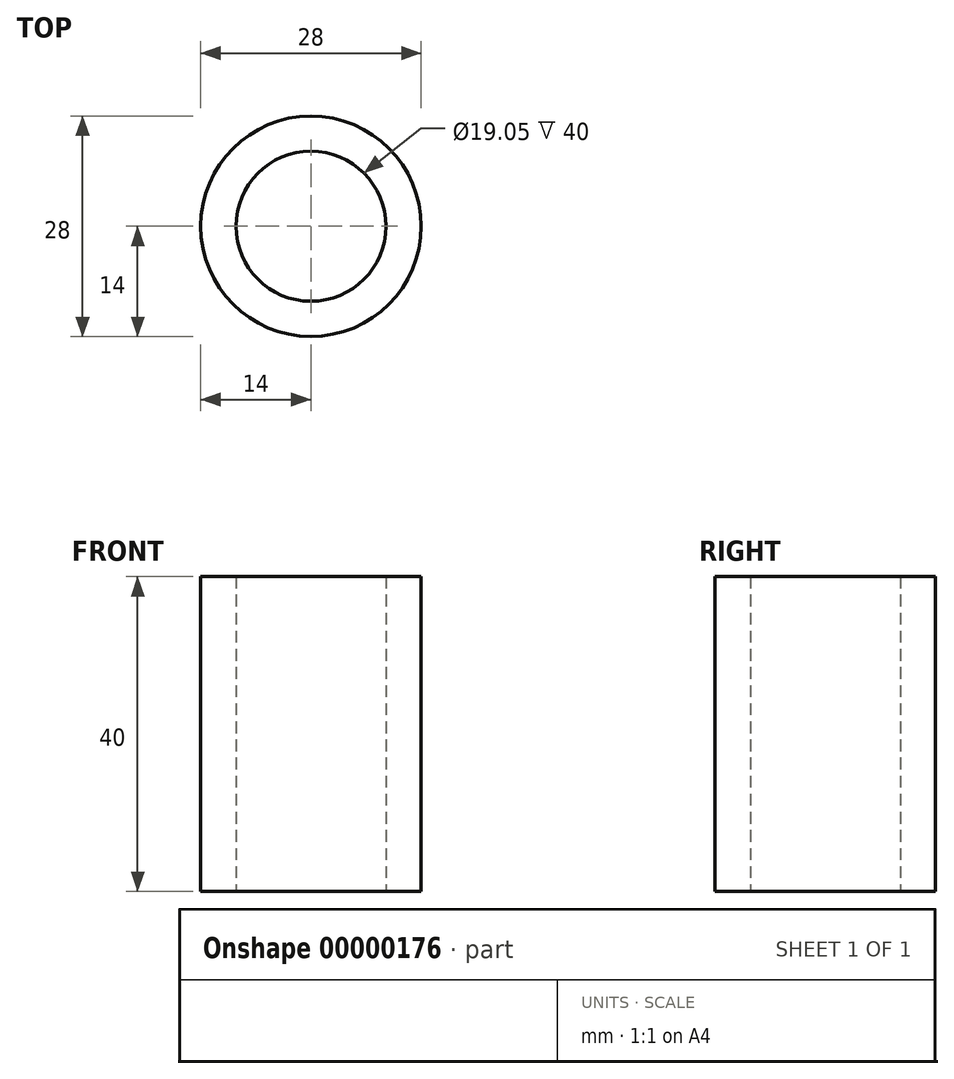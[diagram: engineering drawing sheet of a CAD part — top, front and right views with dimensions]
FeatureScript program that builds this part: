
annotation { "Feature Type Name" : "Feature", "Feature Type Description" : "" }
export const myFeature = defineFeature(function(context is Context, id is Id, definition is map)
    precondition{}
    {
        {
            var Q0;
            Q0=qCreatedBy(makeId("Top.planeOp"),FACE);
            var sketch = newSketch(context, id + "F0", { "sketchPlane" : qUnion([Q0])});
            skCircle(sketch, "E0", {"center": v(0, 0) * mm, "radius": 9.53 * mm});
            skCircle(sketch, "E1", {"center": v(0, 0) * mm, "radius": 14 * mm});
            skSolve(sketch);
        }
        {
            var Q0;
            Q0=makeQuery(id+"F0.imprint","IMPRINT",FACE,{"disambiguationData":[TD([[makeQuery(id+"F0.imprint","IMPRINT",EDGE,{"derivedFrom":sQuery(id+"F0.wireOp",EDGE,"E0")}),-1.0]])]});
            extrude(context, id + "F1", {"entities" : qUnion([Q0]), "depth" : 40 * mm});
        }
    });
